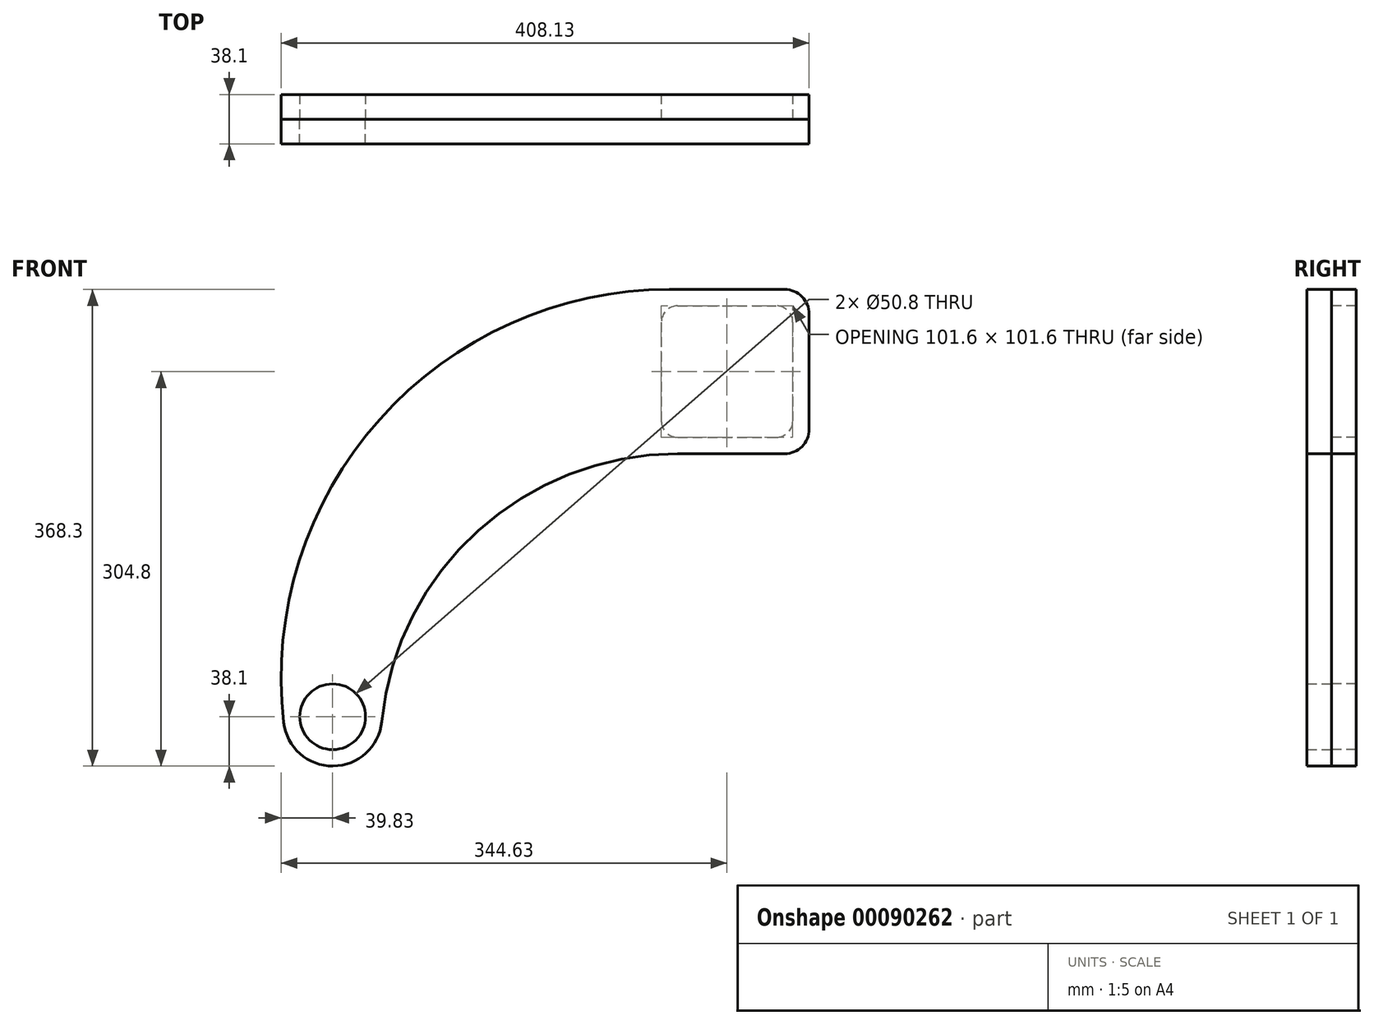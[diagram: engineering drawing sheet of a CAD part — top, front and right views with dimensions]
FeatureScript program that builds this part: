
annotation { "Feature Type Name" : "Feature", "Feature Type Description" : "" }
export const myFeature = defineFeature(function(context is Context, id is Id, definition is map)
    precondition{}
    {
        {
            var Q0;
            Q0=qCreatedBy(makeId("Front.planeOp"),FACE);
            var sketch = newSketch(context, id + "F0", { "sketchPlane" : qUnion([Q0])});
            skLineSegment(sketch, "E0", {"start": v(-107.95, 0) * mm, "end": v(-19.05, 0) * mm});
            skLineSegment(sketch, "E1", {"start": v(0, -19.05) * mm, "end": v(0, -107.95) * mm});
            skArc(sketch, "E2", {"start": v(-406.15, -334.56) * mm, "mid": v(-368.02, -368.3) * mm, "end": v(-330.4, -334) * mm});
            skCircle(sketch, "E3", {"center": v(-368.3, -330.2) * mm, "radius": 25.4 * mm});
            skPoint(sketch, "E4.visualSharp", {"position": v(0, 0) * mm});
            skArc(sketch, "E5.filletArc", {"start": v(0, -19.05) * mm, "mid": v(-5.58, -5.58) * mm, "end": v(-19.05, 0) * mm});
            skLineSegment(sketch, "E6.bottom", {"start": v(-101.6, -12.7) * mm, "end": v(-25.4, -12.7) * mm});
            skLineSegment(sketch, "E6.top", {"start": v(-101.6, -114.3) * mm, "end": v(-25.4, -114.3) * mm});
            skLineSegment(sketch, "E6.left", {"start": v(-114.3, -25.4) * mm, "end": v(-114.3, -101.6) * mm});
            skLineSegment(sketch, "E6.right", {"start": v(-12.7, -25.4) * mm, "end": v(-12.7, -101.6) * mm});
            skLineSegment(sketch, "E7", {"start": v(-63.5, 0) * mm, "end": v(-63.5, -127) * mm, "construction": true});
            skPoint(sketch, "E8", {"position": v(-63.5, -114.3) * mm});
            skPoint(sketch, "E9.visualSharp", {"position": v(-114.3, -12.7) * mm});
            skArc(sketch, "E9.filletArc", {"start": v(-101.6, -12.7) * mm, "mid": v(-110.58, -16.42) * mm, "end": v(-114.3, -25.4) * mm});
            skPoint(sketch, "E10.visualSharp", {"position": v(-12.7, -12.7) * mm});
            skArc(sketch, "E10.filletArc", {"start": v(-12.7, -25.4) * mm, "mid": v(-16.42, -16.42) * mm, "end": v(-25.4, -12.7) * mm});
            skPoint(sketch, "E11.visualSharp", {"position": v(-12.7, -114.3) * mm});
            skArc(sketch, "E11.filletArc", {"start": v(-25.4, -114.3) * mm, "mid": v(-16.42, -110.58) * mm, "end": v(-12.7, -101.6) * mm});
            skPoint(sketch, "E12.visualSharp", {"position": v(-114.3, -114.3) * mm});
            skArc(sketch, "E12.filletArc", {"start": v(-114.3, -101.6) * mm, "mid": v(-110.58, -110.58) * mm, "end": v(-101.6, -114.3) * mm});
            skArc(sketch, "E13", {"start": v(-107.95, 0) * mm, "mid": v(-332.04, -100.45) * mm, "end": v(-406.15, -334.56) * mm});
            skLineSegment(sketch, "E14", {"start": v(-19.05, -127) * mm, "end": v(-101.6, -127) * mm});
            skArc(sketch, "E15", {"start": v(-101.6, -127) * mm, "mid": v(-255.87, -186.43) * mm, "end": v(-330.4, -334) * mm});
            skPoint(sketch, "E16.visualSharp", {"position": v(0, -127) * mm});
            skArc(sketch, "E16.filletArc", {"start": v(-19.05, -127) * mm, "mid": v(-5.58, -121.42) * mm, "end": v(0, -107.95) * mm});
            skSolve(sketch);
        }
        {
            var Q0;
            Q0=makeQuery(id+"F0.imprint","IMPRINT",FACE,{"disambiguationData":[TD([[makeQuery(id+"F0.imprint","IMPRINT",EDGE,{"derivedFrom":sQuery(id+"F0.wireOp",EDGE,"E0")}),-1.0]])]});
            var Q1;
            Q1=makeQuery(id+"F0.imprint","IMPRINT",FACE,{"disambiguationData":[TD([[makeQuery(id+"F0.imprint","IMPRINT",EDGE,{"derivedFrom":sQuery(id+"F0.wireOp",EDGE,"E6.bottom")}),-1.0]])]});
            extrude(context, id + "F1", {"entities" : qUnion([Q0, Q1]), "depth" : 19.05 * mm});
        }
        {
            var Q0;
            Q0=makeQuery(id+"F0.imprint","IMPRINT",FACE,{"disambiguationData":[TD([[makeQuery(id+"F0.imprint","IMPRINT",EDGE,{"derivedFrom":sQuery(id+"F0.wireOp",EDGE,"E0")}),-1.0]])]});
            extrude(context, id + "F2", {"entities" : qUnion([Q0]), "oppositeDirection" : true, "depth" : 19.05 * mm});
        }
    });
